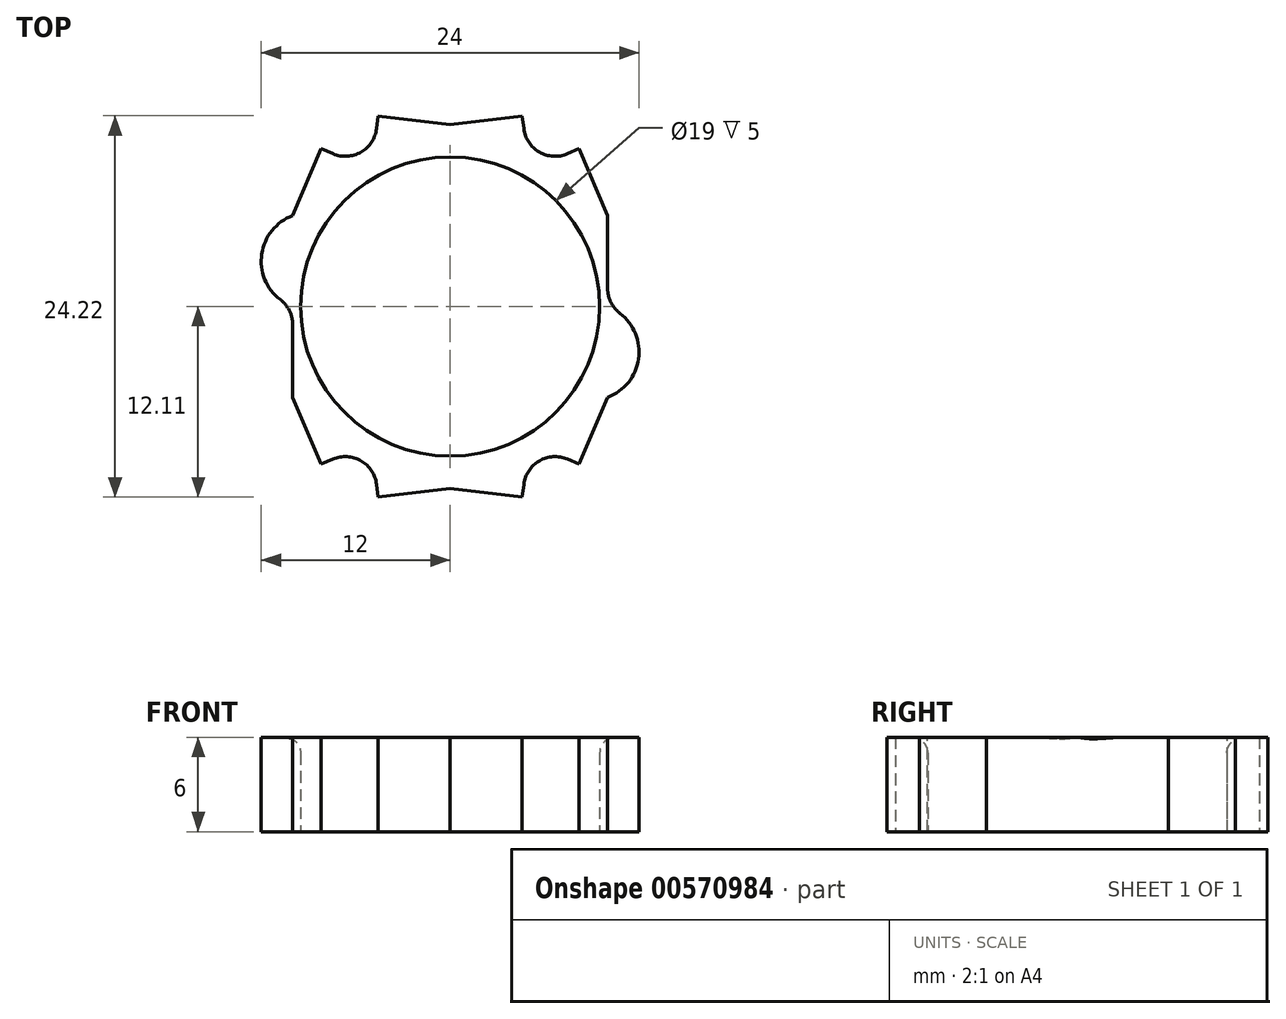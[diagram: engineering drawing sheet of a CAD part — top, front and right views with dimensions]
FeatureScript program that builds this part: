
annotation { "Feature Type Name" : "Feature", "Feature Type Description" : "" }
export const myFeature = defineFeature(function(context is Context, id is Id, definition is map)
    precondition{}
    {
        {
            var Q0;
            Q0=qCreatedBy(makeId("Top.planeOp"),FACE);
            var sketch = newSketch(context, id + "F0", { "sketchPlane" : qUnion([Q0])});
            skLineSegment(sketch, "E0", {"start": v(0, -30) * mm, "end": v(0, 30) * mm, "construction": true});
            skLineSegment(sketch, "E1", {"start": v(-30, 0) * mm, "end": v(30, 0) * mm, "construction": true});
            skCircle(sketch, "E2.cCircle", {"center": v(0, 0) * mm, "radius": 10 * mm, "construction": true});
            skLineSegment(sketch, "E2.0", {"start": v(-10, -5.77) * mm, "end": v(-10, 5.77) * mm});
            skLineSegment(sketch, "E2.1", {"start": v(-10, 5.77) * mm, "end": v(0, 11.55) * mm});
            skLineSegment(sketch, "E2.2", {"start": v(0, 11.55) * mm, "end": v(10, 5.77) * mm});
            skLineSegment(sketch, "E2.3", {"start": v(10, 5.77) * mm, "end": v(10, -5.77) * mm});
            skLineSegment(sketch, "E2.4", {"start": v(10, -5.77) * mm, "end": v(0, -11.55) * mm});
            skLineSegment(sketch, "E2.5", {"start": v(0, -11.55) * mm, "end": v(-10, -5.77) * mm});
            skPoint(sketch, "E2.0.midPoint", {"position": v(-10, 0) * mm});
            skLineSegment(sketch, "E3", {"start": v(-10, 5.77) * mm, "end": v(-8.2, 10.02) * mm});
            skLineSegment(sketch, "E4", {"start": v(-8.2, 10.02) * mm, "end": v(-5, 8.66) * mm});
            skLineSegment(sketch, "E5", {"start": v(-5, 8.66) * mm, "end": v(-4.58, 12.1) * mm});
            skLineSegment(sketch, "E6", {"start": v(-4.58, 12.1) * mm, "end": v(0, 11.55) * mm});
            skArc(sketch, "E7", {"start": v(-10, 5.77) * mm, "mid": v(-12, 2.89) * mm, "end": v(-10, 0) * mm});
            skLineSegment(sketch, "E8.MirrorCS", {"start": v(4.58, 12.1) * mm, "end": v(0, 11.55) * mm});
            skLineSegment(sketch, "E9.MirrorCS", {"start": v(5, 8.66) * mm, "end": v(4.58, 12.1) * mm});
            skLineSegment(sketch, "E10.MirrorCS", {"start": v(8.2, 10.02) * mm, "end": v(5, 8.66) * mm});
            skLineSegment(sketch, "E11.MirrorCS", {"start": v(10, 5.77) * mm, "end": v(8.2, 10.02) * mm});
            skArc(sketch, "E12.MirrorCS", {"start": v(10, 5.77) * mm, "mid": v(12, 2.89) * mm, "end": v(10, 0) * mm});
            skArc(sketch, "E13.MirrorCS", {"start": v(-10, -5.77) * mm, "mid": v(-12, -2.89) * mm, "end": v(-10, 0) * mm});
            skLineSegment(sketch, "E14.MirrorCS", {"start": v(-10, -5.77) * mm, "end": v(-8.2, -10.02) * mm});
            skLineSegment(sketch, "E15.MirrorCS", {"start": v(-8.2, -10.02) * mm, "end": v(-5, -8.66) * mm});
            skLineSegment(sketch, "E16.MirrorCS", {"start": v(-5, -8.66) * mm, "end": v(-4.58, -12.1) * mm});
            skLineSegment(sketch, "E17.MirrorCS", {"start": v(-4.58, -12.1) * mm, "end": v(0, -11.55) * mm});
            skLineSegment(sketch, "E18.MirrorCS", {"start": v(4.58, -12.1) * mm, "end": v(0, -11.55) * mm});
            skLineSegment(sketch, "E19.MirrorCS", {"start": v(5, -8.66) * mm, "end": v(4.58, -12.1) * mm});
            skLineSegment(sketch, "E20.MirrorCS", {"start": v(10, -5.77) * mm, "end": v(8.2, -10.02) * mm});
            skLineSegment(sketch, "E21.MirrorCS", {"start": v(8.2, -10.02) * mm, "end": v(5, -8.66) * mm});
            skArc(sketch, "E22.MirrorCS", {"start": v(10, -5.77) * mm, "mid": v(12, -2.89) * mm, "end": v(10, 0) * mm});
            skSolve(sketch);
        }
        {
            var Q0;
            {var subQ0=sQuery(id+"F0.wireOp",EDGE,"E3");Q0=makeQuery(id+"F0.imprint","IMPRINT",FACE,{"disambiguationData":[TD([[makeQuery(id+"F0.imprint","IMPRINT",EDGE,{"derivedFrom":subQ0}),-1.0]])]});}
            var Q1;
            {var subQ0=sQuery(id+"F0.wireOp",EDGE,"E7");Q1=makeQuery(id+"F0.imprint","IMPRINT",FACE,{"disambiguationData":[TD([[makeQuery(id+"F0.imprint","IMPRINT",EDGE,{"derivedFrom":subQ0}),1.0]])]});}
            var Q2;
            {var subQ0=sQuery(id+"F0.wireOp",EDGE,"E13.MirrorCS");Q2=makeQuery(id+"F0.imprint","IMPRINT",FACE,{"disambiguationData":[TD([[makeQuery(id+"F0.imprint","IMPRINT",EDGE,{"derivedFrom":subQ0}),-1.0]])]});}
            var Q3;
            {var subQ2=sQuery(id+"F0.wireOp",EDGE,"E5");Q3=makeQuery(id+"F0.imprint","IMPRINT",FACE,{"disambiguationData":[TD([[makeQuery(id+"F0.imprint","IMPRINT",EDGE,{"derivedFrom":subQ2}),-1.0]])]});}
            var Q4;
            {var subQ0=sQuery(id+"F0.wireOp",EDGE,"E8.MirrorCS");Q4=makeQuery(id+"F0.imprint","IMPRINT",FACE,{"disambiguationData":[TD([[makeQuery(id+"F0.imprint","IMPRINT",EDGE,{"derivedFrom":subQ0}),1.0]])]});}
            var Q5;
            {var subQ2=sQuery(id+"F0.wireOp",EDGE,"E16.MirrorCS");Q5=makeQuery(id+"F0.imprint","IMPRINT",FACE,{"disambiguationData":[TD([[makeQuery(id+"F0.imprint","IMPRINT",EDGE,{"derivedFrom":subQ2}),1.0]])]});}
            var Q6;
            {var subQ2=sQuery(id+"F0.wireOp",EDGE,"E10.MirrorCS");Q6=makeQuery(id+"F0.imprint","IMPRINT",FACE,{"disambiguationData":[TD([[makeQuery(id+"F0.imprint","IMPRINT",EDGE,{"derivedFrom":subQ2}),1.0]])]});}
            var Q7;
            {var subQ0=sQuery(id+"F0.wireOp",EDGE,"E22.MirrorCS");Q7=makeQuery(id+"F0.imprint","IMPRINT",FACE,{"disambiguationData":[TD([[makeQuery(id+"F0.imprint","IMPRINT",EDGE,{"derivedFrom":subQ0}),1.0]])]});}
            var Q8;
            {var subQ0=sQuery(id+"F0.wireOp",EDGE,"E12.MirrorCS");Q8=makeQuery(id+"F0.imprint","IMPRINT",FACE,{"disambiguationData":[TD([[makeQuery(id+"F0.imprint","IMPRINT",EDGE,{"derivedFrom":subQ0}),-1.0]])]});}
            var Q9;
            {var subQ0=sQuery(id+"F0.wireOp",EDGE,"E14.MirrorCS");Q9=makeQuery(id+"F0.imprint","IMPRINT",FACE,{"disambiguationData":[TD([[makeQuery(id+"F0.imprint","IMPRINT",EDGE,{"derivedFrom":subQ0}),1.0]])]});}
            var Q10;
            {var subQ0=sQuery(id+"F0.wireOp",EDGE,"E18.MirrorCS");Q10=makeQuery(id+"F0.imprint","IMPRINT",FACE,{"disambiguationData":[TD([[makeQuery(id+"F0.imprint","IMPRINT",EDGE,{"derivedFrom":subQ0}),-1.0]])]});}
            var Q11;
            {var subQ0=sQuery(id+"F0.wireOp",EDGE,"E20.MirrorCS");Q11=makeQuery(id+"F0.imprint","IMPRINT",FACE,{"disambiguationData":[TD([[makeQuery(id+"F0.imprint","IMPRINT",EDGE,{"derivedFrom":subQ0}),-1.0]])]});}
            var Q12;
            {var subQ14=sQuery(id+"F0.wireOp",EDGE,"E13.MirrorCS");var subQ15=sQuery(id+"F0.wireOp",EDGE,"E2.0");var subQ17=sQuery(id+"F0.wireOp",EDGE,"E7");var subQ18=makeQuery(id+"F0.imprint","INTERSECT",VERTEX,{"derivedFrom":[subQ15,subQ17,subQ14]});Q12=makeQuery(id+"F0.imprint","IMPRINT",FACE,{"disambiguationData":[TD([[makeQuery(id+"F0.imprint","IMPRINT",EDGE,{"disambiguationData":[TD([[subQ18,1.0]])],"derivedFrom":subQ15}),-1.0]])]});}
            extrude(context, id + "F1", {"entities" : qUnion([Q0, Q1, Q2, Q3, Q4, Q5, Q6, Q7, Q8, Q9, Q10, Q11, Q12]), "depth" : 6 * mm, "offsetDistance" : 25 * mm});
        }
        {
            var Q0;
            Q0=makeQuery(id+"F1.opExtrude","CAP_FACE",FACE,{"disambiguationData":[OSD([sQuery(id+"F0.wireOp",EDGE,"E3"),sQuery(id+"F0.wireOp",EDGE,"E4"),sQuery(id+"F0.wireOp",EDGE,"E5"),sQuery(id+"F0.wireOp",EDGE,"E6"),sQuery(id+"F0.wireOp",EDGE,"E7"),sQuery(id+"F0.wireOp",EDGE,"E8.MirrorCS"),sQuery(id+"F0.wireOp",EDGE,"E9.MirrorCS"),sQuery(id+"F0.wireOp",EDGE,"E10.MirrorCS"),sQuery(id+"F0.wireOp",EDGE,"E11.MirrorCS"),sQuery(id+"F0.wireOp",EDGE,"E12.MirrorCS"),sQuery(id+"F0.wireOp",EDGE,"E13.MirrorCS"),sQuery(id+"F0.wireOp",EDGE,"E14.MirrorCS"),sQuery(id+"F0.wireOp",EDGE,"E15.MirrorCS"),sQuery(id+"F0.wireOp",EDGE,"E16.MirrorCS"),sQuery(id+"F0.wireOp",EDGE,"E17.MirrorCS"),sQuery(id+"F0.wireOp",EDGE,"E18.MirrorCS"),sQuery(id+"F0.wireOp",EDGE,"E19.MirrorCS"),sQuery(id+"F0.wireOp",EDGE,"E20.MirrorCS"),sQuery(id+"F0.wireOp",EDGE,"E21.MirrorCS"),sQuery(id+"F0.wireOp",EDGE,"E22.MirrorCS")])],"isStart":true});
            var sketch = newSketch(context, id + "F2", { "sketchPlane" : qUnion([Q0])});
            skCircle(sketch, "E23", {"center": v(0, 0) * mm, "radius": 9.5 * mm});
            skSolve(sketch);
        }
        {
            var Q0;
            Q0=makeQuery(id+"F2.imprint","IMPRINT",FACE,{"disambiguationData":[TD([[makeQuery(id+"F2.imprint","IMPRINT",EDGE,{"derivedFrom":sQuery(id+"F2.wireOp",EDGE,"E23")}),1.0]])]});
            extrude(context, id + "F3", {"entities" : qUnion([Q0]), "operationType" : NewBodyOperationType.REMOVE, "oppositeDirection" : true, "depth" : 7 * mm, "offsetDistance" : 25 * mm});
        }
        {
            var Q0;
            Q0=makeQuery(id+"F1.opExtrude","SWEPT_EDGE",EDGE,{"disambiguationData":[OSD([sQuery(id+"F0.wireOp",EDGE,"E2.2"),sQuery(id+"F0.wireOp",EDGE,"E9.MirrorCS"),sQuery(id+"F0.wireOp",EDGE,"E10.MirrorCS")])]});
            var Q1;
            Q1=makeQuery(id+"F1.opExtrude","SWEPT_EDGE",EDGE,{"disambiguationData":[OSD([sQuery(id+"F0.wireOp",EDGE,"E2.1"),sQuery(id+"F0.wireOp",EDGE,"E4"),sQuery(id+"F0.wireOp",EDGE,"E5")])]});
            var Q2;
            Q2=makeQuery(id+"F1.opExtrude","SWEPT_EDGE",EDGE,{"disambiguationData":[OSD([sQuery(id+"F0.wireOp",EDGE,"E2.4"),sQuery(id+"F0.wireOp",EDGE,"E19.MirrorCS"),sQuery(id+"F0.wireOp",EDGE,"E21.MirrorCS")])]});
            var Q3;
            Q3=makeQuery(id+"F1.opExtrude","SWEPT_EDGE",EDGE,{"disambiguationData":[OSD([sQuery(id+"F0.wireOp",EDGE,"E2.5"),sQuery(id+"F0.wireOp",EDGE,"E15.MirrorCS"),sQuery(id+"F0.wireOp",EDGE,"E16.MirrorCS")])]});
            var Q4;
            Q4=makeQuery(id+"F1.opExtrude","SWEPT_EDGE",EDGE,{"disambiguationData":[OSD([sQuery(id+"F0.wireOp",EDGE,"E2.3"),sQuery(id+"F0.wireOp",EDGE,"E12.MirrorCS"),sQuery(id+"F0.wireOp",EDGE,"E22.MirrorCS")])]});
            var Q5;
            Q5=makeQuery(id+"F1.opExtrude","SWEPT_EDGE",EDGE,{"disambiguationData":[OSD([sQuery(id+"F0.wireOp",EDGE,"E2.0"),sQuery(id+"F0.wireOp",EDGE,"E7"),sQuery(id+"F0.wireOp",EDGE,"E13.MirrorCS")])]});
            fillet(context, id + "F4", {"entities" : qUnion([Q0, Q1, Q2, Q3, Q4, Q5]), "radius" : 2 * mm, "tangentPropagation" : true, "allowEdgeOverflow" : false});
        }
        {
            var Q0;
            Q0=makeQuery(id+"F3.boolean.opBoolean","INTERSECT",EDGE,{"derivedFrom":[makeQuery(id+"F1.opExtrude","CAP_FACE",FACE,{"disambiguationData":[OSD([sQuery(id+"F0.wireOp",EDGE,"E3"),sQuery(id+"F0.wireOp",EDGE,"E4"),sQuery(id+"F0.wireOp",EDGE,"E5"),sQuery(id+"F0.wireOp",EDGE,"E6"),sQuery(id+"F0.wireOp",EDGE,"E7"),sQuery(id+"F0.wireOp",EDGE,"E8.MirrorCS"),sQuery(id+"F0.wireOp",EDGE,"E9.MirrorCS"),sQuery(id+"F0.wireOp",EDGE,"E10.MirrorCS"),sQuery(id+"F0.wireOp",EDGE,"E11.MirrorCS"),sQuery(id+"F0.wireOp",EDGE,"E12.MirrorCS"),sQuery(id+"F0.wireOp",EDGE,"E13.MirrorCS"),sQuery(id+"F0.wireOp",EDGE,"E14.MirrorCS"),sQuery(id+"F0.wireOp",EDGE,"E15.MirrorCS"),sQuery(id+"F0.wireOp",EDGE,"E16.MirrorCS"),sQuery(id+"F0.wireOp",EDGE,"E17.MirrorCS"),sQuery(id+"F0.wireOp",EDGE,"E18.MirrorCS"),sQuery(id+"F0.wireOp",EDGE,"E19.MirrorCS"),sQuery(id+"F0.wireOp",EDGE,"E20.MirrorCS"),sQuery(id+"F0.wireOp",EDGE,"E21.MirrorCS"),sQuery(id+"F0.wireOp",EDGE,"E22.MirrorCS")])],"isStart":false}),makeQuery(id+"F3.opExtrude","SWEPT_FACE",FACE,{"disambiguationData":[OSD([sQuery(id+"F2.wireOp",EDGE,"E23")])]})]});
            var Q1;
            Q1=makeQuery(id+"F3.boolean.opBoolean","COPY",EDGE,{"derivedFrom":makeQuery(id+"F3.opExtrude","CAP_EDGE",EDGE,{"disambiguationData":[OSD([sQuery(id+"F2.wireOp",EDGE,"E23")])],"isStart":true})});
            fillet(context, id + "F5", {"entities" : qUnion([Q0, Q1]), "radius" : 1 * mm, "tangentPropagation" : true, "allowEdgeOverflow" : false});
        }
    });
